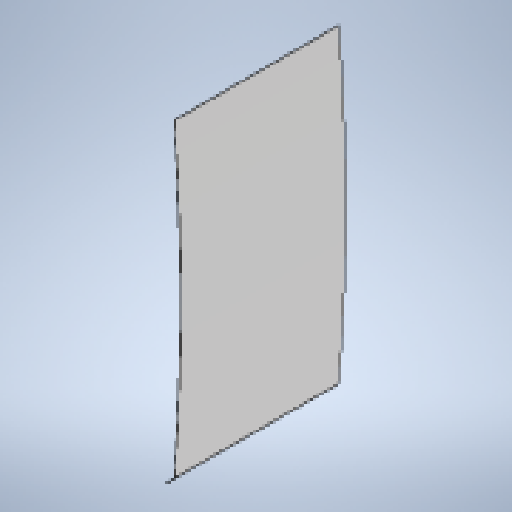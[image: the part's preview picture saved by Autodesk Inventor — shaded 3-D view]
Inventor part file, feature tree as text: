
AUTODESK INVENTOR PART (.ipt)
format: ipt  version: 2025 (Build 290162010, 162A)  size: 315,392 bytes
history: native  units: mm
features: other x4, sheet_metal_op x3, sketch x2
ambient origin geometry x8: Origin, YZ Plane, XZ Plane, XY Plane, X Axis, Y Axis, Z Axis, Center Point
bodies: Body1 (feature_tree)
feature tree (9):
  sheet_metal_op  "Contour Flange2"
  other  "Mark2"
  other  "A-Side Definition"
  sketch  "Sketch1"  dims[d36=3.0mm]
  other  "Plate2"
  sheet_metal_op  "Bend2"
  sheet_metal_op  "Corner2"
  sketch  "Sketch4"  dims[d37=3.0mm d38=1.5mm d39=6.0mm d40=5.0mm d41=980.0mm d42=5.0mm d43=3.0mm d44=12.0mm d45=3.0mm d46=5.0mm d65=8.0mm d78=3.0mm d80=3.0mm d121=5.0mm d122=63.0mm d123=11050.0mm d124=23.736478mm d125=1843.0mm d126=5.0mm d127=12.0mm d128=12.0mm d130=0.0mm]
  other  "Definition1"
